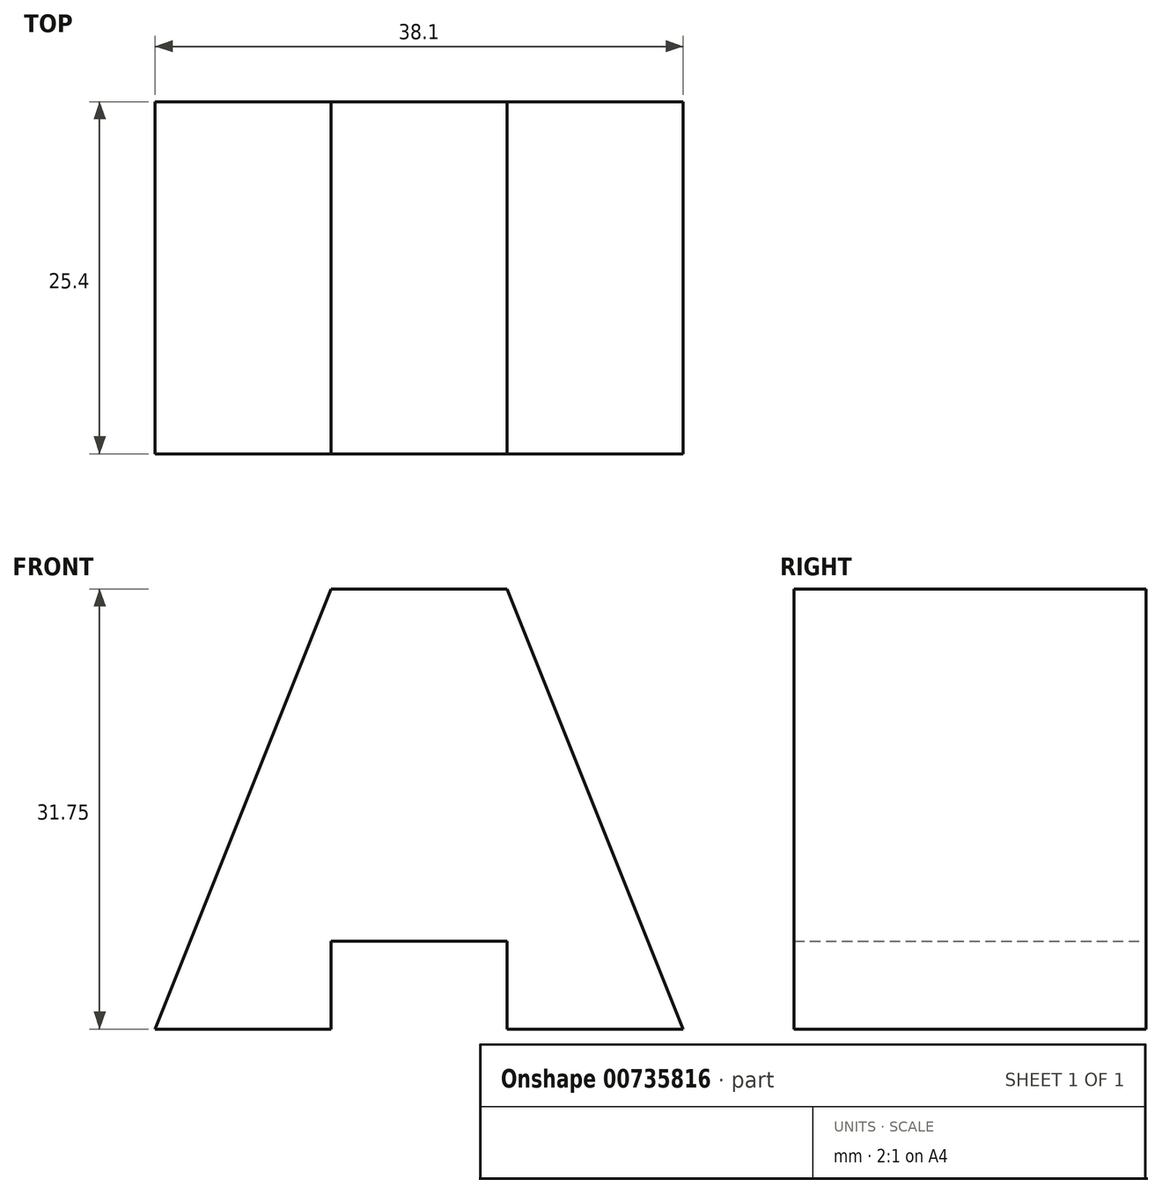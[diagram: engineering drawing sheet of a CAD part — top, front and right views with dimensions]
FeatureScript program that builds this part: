
annotation { "Feature Type Name" : "Feature", "Feature Type Description" : "" }
export const myFeature = defineFeature(function(context is Context, id is Id, definition is map)
    precondition{}
    {
        {
            var Q0;
            Q0=qCreatedBy(makeId("Front.planeOp"),FACE);
            var sketch = newSketch(context, id + "F0", { "sketchPlane" : qUnion([Q0])});
            skLineSegment(sketch, "E0", {"start": v(0, 0) * mm, "end": v(12.7, 0) * mm});
            skLineSegment(sketch, "E1", {"start": v(12.7, 0) * mm, "end": v(12.7, 6.35) * mm});
            skLineSegment(sketch, "E2", {"start": v(12.7, 6.35) * mm, "end": v(25.4, 6.35) * mm});
            skLineSegment(sketch, "E3", {"start": v(25.4, 6.35) * mm, "end": v(25.4, 0) * mm});
            skLineSegment(sketch, "E4", {"start": v(25.4, 0) * mm, "end": v(38.1, 0) * mm});
            skLineSegment(sketch, "E5", {"start": v(38.1, 0) * mm, "end": v(25.4, 31.75) * mm});
            skLineSegment(sketch, "E6", {"start": v(25.4, 31.75) * mm, "end": v(12.7, 31.75) * mm});
            skLineSegment(sketch, "E7", {"start": v(12.7, 31.75) * mm, "end": v(0, 0) * mm});
            skSolve(sketch);
        }
        {
            var Q0;
            Q0 = qSketchRegion(id + "F0", true);
            extrude(context, id + "F1", {"entities" : qUnion([Q0]), "depth" : 25.4 * mm, "offsetDistance" : 25.4 * mm});
        }
    });
